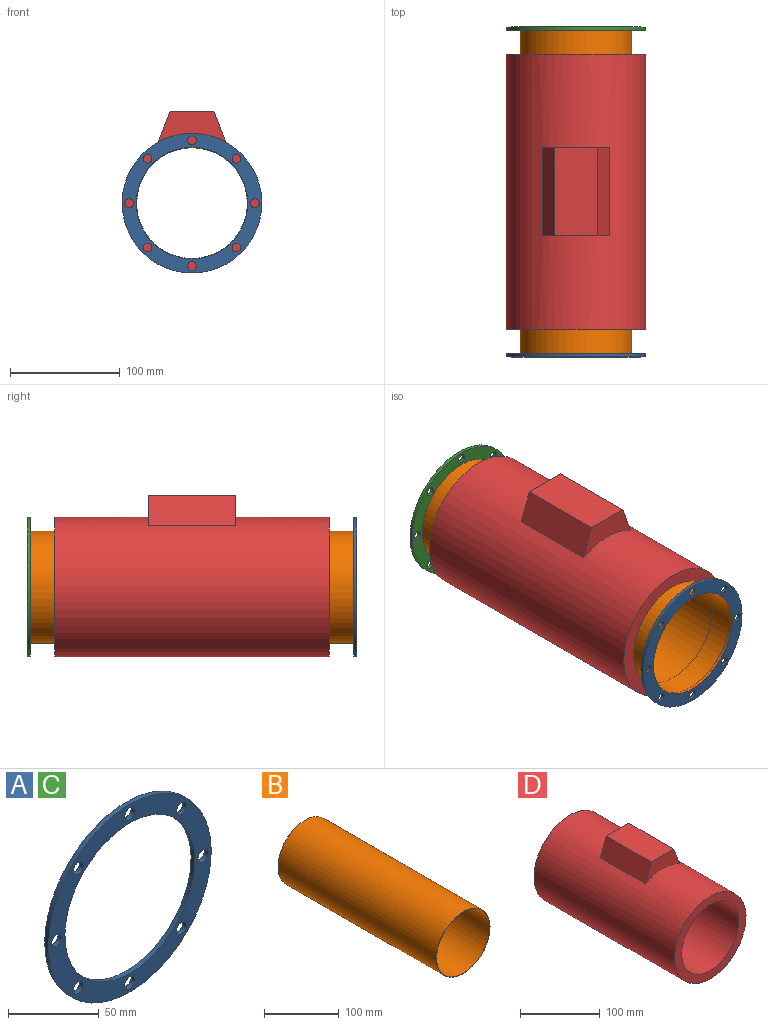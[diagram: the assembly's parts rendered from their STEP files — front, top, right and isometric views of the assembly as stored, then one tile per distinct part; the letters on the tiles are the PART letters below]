
ASSEMBLY  parts=4 mates=3
PART A: 12 faces, bbox 127x3x127 mm
  f0: cylinder r=50.8mm len=101.6mm, axis (0,1,0), area 957.6mm2, adj f10,f11
  f1: cylinder r=4mm len=8mm, axis (0,1,0), area 75.4mm2, adj f10,f11
  f2: cylinder r=4mm len=8mm, axis (0,1,0), area 75.4mm2, adj f10,f11
  f3: cylinder r=4mm len=8mm, axis (0,1,0), area 75.4mm2, adj f10,f11
  f4: cylinder r=4mm len=8mm, axis (0,1,0), area 75.4mm2, adj f10,f11
  f5: cylinder r=4mm len=8mm, axis (0,1,0), area 75.4mm2, adj f10,f11
  f6: cylinder r=4mm len=8mm, axis (0,1,0), area 75.4mm2, adj f10,f11
  f7: cylinder r=4mm len=8mm, axis (0,1,0), area 75.4mm2, adj f10,f11
  f8: cylinder r=4mm len=8mm, axis (0,1,0), area 75.4mm2, adj f10,f11
  f9: cylinder r=63.5mm len=127mm, axis (0,1,0), area 1196.9mm2, adj f10,f11
  f10: plane 127x127mm, normal (0,-1,0), area 4158.2mm2, adj f0,f1,f2,f3,f4,f5,f6,f7
  f11: plane 127x127mm, normal (0,1,0), area 4158.2mm2, adj f0,f1,f2,f3,f4,f5,f6,f7
PART B: 4 faces, bbox 101.6x300x101.6 mm
  f0: cylinder r=50.3mm len=300mm, axis (0,1,0), area 94813.3mm2, adj f2,f3
  f1: cylinder r=50.8mm len=300mm, axis (0,1,0), area 95755.7mm2, adj f2,f3
  f2: plane 101.6x101.6mm, normal (0,-1,0), area 158.8mm2, adj f0,f1
  f3: plane 101.6x101.6mm, normal (0,1,0), area 158.8mm2, adj f0,f1
PART C: same geometry as A
PART D: 9 faces, bbox 127x250x147.3 mm
  f0: cylinder r=63.5mm len=250mm, axis (0,1,0), area 94649.5mm2, adj f2,f3,f5,f6,f7,f8
  f1: cylinder r=50.8mm len=250mm, axis (0,1,0), area 79796.5mm2, adj f2,f3
  f2: plane 127x127mm, normal (0,-1,0), area 4560.4mm2, adj f0,f1
  f3: plane 127x127mm, normal (0,1,0), area 4560.4mm2, adj f0,f1
  f4: plane 80x40mm, normal (0,0,1), area 3200mm2, adj f5,f6,f7,f8
  f5: plane 80x28.09mm, normal (-0.94,0,0.35), area 2400mm2, adj f0,f4,f7,f8
  f6: plane 80x28.09mm, normal (0.94,0,0.35), area 2400mm2, adj f0,f4,f7,f8
  f7: plane 61.06x28.09mm, normal (0,-1,0), area 1096.9mm2, adj f0,f4,f5,f6
  f8: plane 61.06x28.09mm, normal (0,1,0), area 1096.9mm2, adj f0,f4,f5,f6
PLACE A t=(-111.44,-170.1,61.86)mm
PLACE B t=(-111.44,126.9,61.86)mm
PLACE C t=(-111.44,126.9,61.86)mm
PLACE D t=(-111.44,-23.1,61.86)mm
MATE fastened D.f1 <-> B.f0  axis (0,-1,0) through (-111.44,-148.1,61.86)mm
MATE fastened A.f0 <-> B.f0  axis (0,-1,0) through (-111.44,-173.1,61.86)mm
MATE fastened C.f0 <-> B.f0  axis (0,1,0) through (-111.44,126.9,61.86)mm
